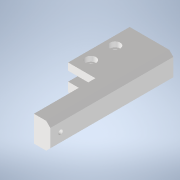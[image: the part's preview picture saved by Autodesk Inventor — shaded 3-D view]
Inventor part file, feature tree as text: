
AUTODESK INVENTOR PART (.ipt)
format: ipt  version: 2020 (Build 240168000, 168)  size: 168,448 bytes
history: native  units: mm
features: other x3, sketch x3, extrude x2, hole x1
ambient origin geometry x8: Origin, YZ Plane, XZ Plane, XY Plane, X Axis, Y Axis, Z Axis, Center Point
bodies: Volumenkörper1 (feature_tree)
feature tree (9):
  other  "GlassesInterface.ipt"
  extrude  "Extrusion1"  Depth=8.0mm
  hole  "Bohrung1"  [1 undecoded]
  extrude  "Extrusion2"  Depth=2.0mm
  other  "Volumenkörper1::GlassesInterface.ipt"
  other  "Bezeichnung1"
  sketch  "Skizze1"  dims[d0=100.0mm d1=8.0mm]
  sketch  "Skizze2"  dims[d2=2.0mm d3=2.0mm]
  sketch  "Skizze3"  dims[d4=2.0mm d5=2.0mm d6=60.0mm d7=0.0mm d8=6.3mm d10=5.0mm d11=2.2mm d12=6.0mm d13=4.0mm d14=2.0mm d15=90.0deg d16=8.0mm d17=20.594885mm d18=4.0mm d19=2.0mm d20=0.0mm]
note: 1 required parameter value undecoded (feature->parameter linkage not recoverable at this tier; creation-order binding heuristic only, values carry confidence <= 0.55)
